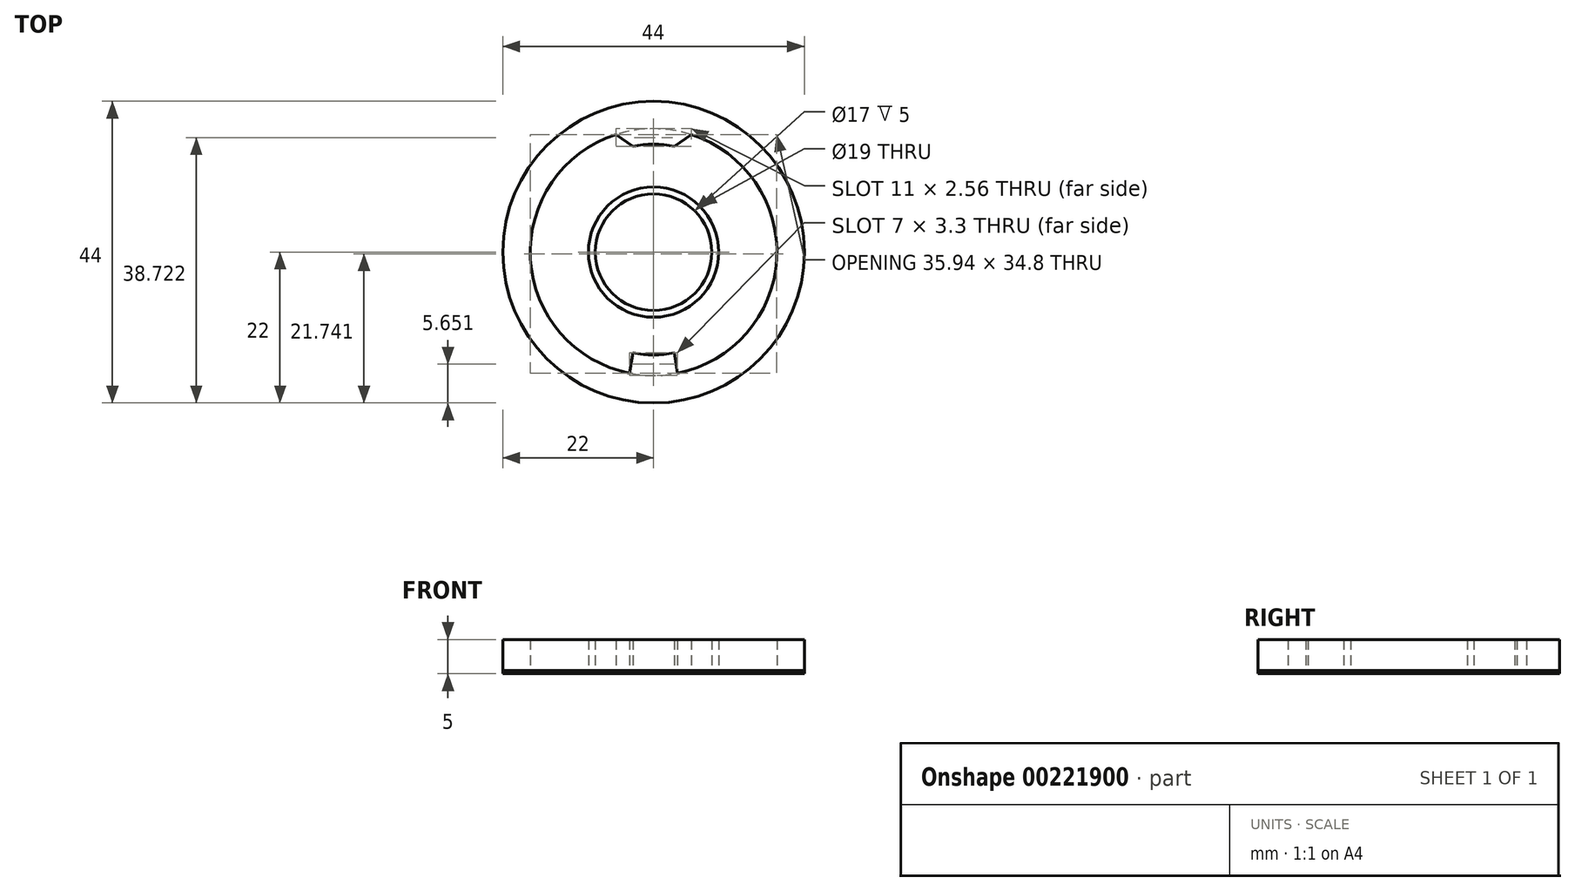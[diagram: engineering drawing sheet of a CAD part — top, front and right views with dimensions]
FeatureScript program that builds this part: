
annotation { "Feature Type Name" : "Feature", "Feature Type Description" : "" }
export const myFeature = defineFeature(function(context is Context, id is Id, definition is map)
    precondition{}
    {
        {
            var Q0;
            Q0=qCreatedBy(makeId("Top.planeOp"),FACE);
            var sketch = newSketch(context, id + "F0", { "sketchPlane" : qUnion([Q0])});
            skCircle(sketch, "E0", {"center": v(0, 0) * mm, "radius": 18 * mm});
            skCircle(sketch, "E1", {"center": v(0, 0) * mm, "radius": 9.5 * mm});
            skLineSegment(sketch, "E2", {"start": v(3.03, 15.44) * mm, "end": v(5.5, 17.14) * mm});
            skLineSegment(sketch, "E3", {"start": v(-3.03, 15.44) * mm, "end": v(-5.5, 17.14) * mm});
            skLineSegment(sketch, "E4", {"start": v(3.03, 15.44) * mm, "end": v(3.03, 14.95) * mm, "construction": true});
            skLineSegment(sketch, "E5", {"start": v(3.03, 14.95) * mm, "end": v(0, 14.95) * mm, "construction": true});
            skLineSegment(sketch, "E6", {"start": v(-3.03, 15.44) * mm, "end": v(-3.03, 14.95) * mm, "construction": true});
            skLineSegment(sketch, "E7", {"start": v(-3.03, 14.95) * mm, "end": v(0, 14.95) * mm, "construction": true});
            skLineSegment(sketch, "E8", {"start": v(5.5, 17.14) * mm, "end": v(0, 17.14) * mm, "construction": true});
            skLineSegment(sketch, "E9", {"start": v(0, 17.14) * mm, "end": v(-5.5, 17.14) * mm, "construction": true});
            skArc(sketch, "E10", {"start": v(3.03, 15.44) * mm, "mid": v(0, 15.74) * mm, "end": v(-3.03, 15.44) * mm});
            skLineSegment(sketch, "E11", {"start": v(3, -14.7) * mm, "end": v(3.5, -17.66) * mm});
            skLineSegment(sketch, "E12", {"start": v(-3, -14.7) * mm, "end": v(-3.5, -17.66) * mm});
            skLineSegment(sketch, "E13", {"start": v(-3.5, -17.66) * mm, "end": v(0, -17.66) * mm, "construction": true});
            skLineSegment(sketch, "E14", {"start": v(0, -17.66) * mm, "end": v(3.5, -17.66) * mm, "construction": true});
            skLineSegment(sketch, "E15", {"start": v(-3, -14.7) * mm, "end": v(-3, -12.96) * mm, "construction": true});
            skLineSegment(sketch, "E16", {"start": v(-3, -12.96) * mm, "end": v(0, -12.96) * mm, "construction": true});
            skLineSegment(sketch, "E17", {"start": v(0, -12.96) * mm, "end": v(3, -12.96) * mm, "construction": true});
            skLineSegment(sketch, "E18", {"start": v(3, -12.96) * mm, "end": v(3, -14.7) * mm, "construction": true});
            skArc(sketch, "E19", {"start": v(-3, -14.7) * mm, "mid": v(0, -15) * mm, "end": v(3, -14.7) * mm});
            skCircle(sketch, "E20", {"center": v(0, 0) * mm, "radius": 8.5 * mm});
            skCircle(sketch, "E21", {"center": v(0, 0) * mm, "radius": 22 * mm});
            skSolve(sketch);
        }
        {
            var Q0;
            Q0 = qSketchRegion(id + "F0", true);
            var Q1;
            {var subQ0=sQuery(id+"F0.wireOp",EDGE,"E2");Q1=makeQuery(id+"F0.imprint","IMPRINT",FACE,{"disambiguationData":[TD([[makeQuery(id+"F0.imprint","IMPRINT",EDGE,{"derivedFrom":subQ0}),1.0]])]});}
            var Q2;
            {var subQ0=sQuery(id+"F0.wireOp",EDGE,"E11");Q2=makeQuery(id+"F0.imprint","IMPRINT",FACE,{"disambiguationData":[TD([[makeQuery(id+"F0.imprint","IMPRINT",EDGE,{"derivedFrom":subQ0}),-1.0]])]});}
            var Q3;
            Q3=makeQuery(id+"F0.imprint","IMPRINT",FACE,{"disambiguationData":[TD([[makeQuery(id+"F0.imprint","IMPRINT",EDGE,{"derivedFrom":sQuery(id+"F0.wireOp",EDGE,"E1")}),1.0]])]});
            extrude(context, id + "F1", {"entities" : qUnion([Q0, Q1, Q2, Q3]), "depth" : 5 * mm});
        }
        {
            var Q0;
            Q0 = qSketchRegion(id + "F0", true);
            var Q1;
            Q1=makeQuery(id+"F0.imprint","IMPRINT",FACE,{"disambiguationData":[TD([[makeQuery(id+"F0.imprint","IMPRINT",EDGE,{"derivedFrom":sQuery(id+"F0.wireOp",EDGE,"E1")}),-1.0]])]});
            var Q2;
            Q2=makeQuery(id+"F0.imprint","IMPRINT",FACE,{"disambiguationData":[TD([[makeQuery(id+"F0.imprint","IMPRINT",EDGE,{"derivedFrom":sQuery(id+"F0.wireOp",EDGE,"E20")}),1.0]])]});
            extrude(context, id + "F2", {"entities" : qUnion([Q0, Q1, Q2]), "depth" : 0.5 * mm});
        }
    });
